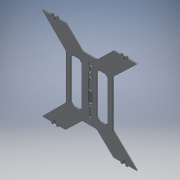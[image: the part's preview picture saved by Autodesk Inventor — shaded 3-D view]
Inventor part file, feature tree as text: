
AUTODESK INVENTOR PART (.ipt)
format: ipt  version: 2019 (Build 230136000, 136)  size: 684,544 bytes
history: native  units: in
note: dims shown in document units (in); Inventor stores cm internally (conversion verified against a paired STEP export)
features: reference x10, other x7, extrude x6, sketch x6, projected_geometry x2, fillet x1, chamfer x1, helix x1
ambient origin geometry x8: Origin, YZ Plane, XZ Plane, XY Plane, X Axis, Y Axis, Z Axis, Center Point
bodies: Solid1 (feature_tree)
feature tree (34):
  extrude  "Extrusion1"  Depth=3.937in
  fillet  "Fillet1"  Radius=3.937in
  extrude  "Extrusion2"  Depth=3.937in
  extrude  "Extrusion3"  Depth=3.937in
  extrude  "Extrusion4"  Depth=2.7559in
  extrude  "Extrusion5"  Depth=0.1575in
  chamfer  "Chamfer1"  Distance=1.0in
  extrude  "Extrusion6"  Depth=0.7874in TaperAngle=0.0deg
  sketch  "Sketch1"  dims[d0=3.937in d1=3.937in d2=3.937in d3=3.937in]
  reference  "Reference1"
  reference  "Reference2"
  sketch  "Sketch2"  dims[d4=4.106in d5=3.937in]
  sketch  "Sketch3"  dims[d6=3.937in d7=3.937in]
  reference  "Reference3"
  reference  "Reference4"
  reference  "Reference5"
  reference  "Reference6"
  sketch  "Sketch4"  dims[d8=2.7559in d9=2.7559in]
  reference  "Reference7"
  reference  "Reference8"
  reference  "Reference9"
  reference  "Reference10"
  sketch  "Sketch5"  dims[d10=0.1575in d11=0.0in d12=0.3937in d13=1.0in d14=0.0in]
  projected_geometry  "Projected Loop1"
  sketch  "Sketch6"  dims[d15=1.0in d16=0.0in d17=1.0in d18=0.0in d19=0.7874in d20=0.7874in d21=1.0in d22=0.0in d23=0.4375in d24=0.125in d25=45.0deg d26=0.0079in d27=0.0079in d28=0.0079in d29=1.0in d30=0.0in]
  projected_geometry  "Projected Loop2"
  other  "<userpath>\Documents\CAD Files\Helix DLP\Helix DLP Z Stage.iam"
  helix  "Helix DLP Z Stage.iam"  [1 undecoded]
  other  "Z stage_side:1"
  other  "Z stage_side:2"
  other  "Maker_jigsaw_template:2"
  other  "Maker_jigsaw_template:3"
  other  "Maker_jigsaw_template:1"
  other  "Maker_jigsaw_template:4"
note: 1 required parameter value undecoded (feature->parameter linkage not recoverable at this tier; creation-order binding heuristic only, values carry confidence <= 0.55)
